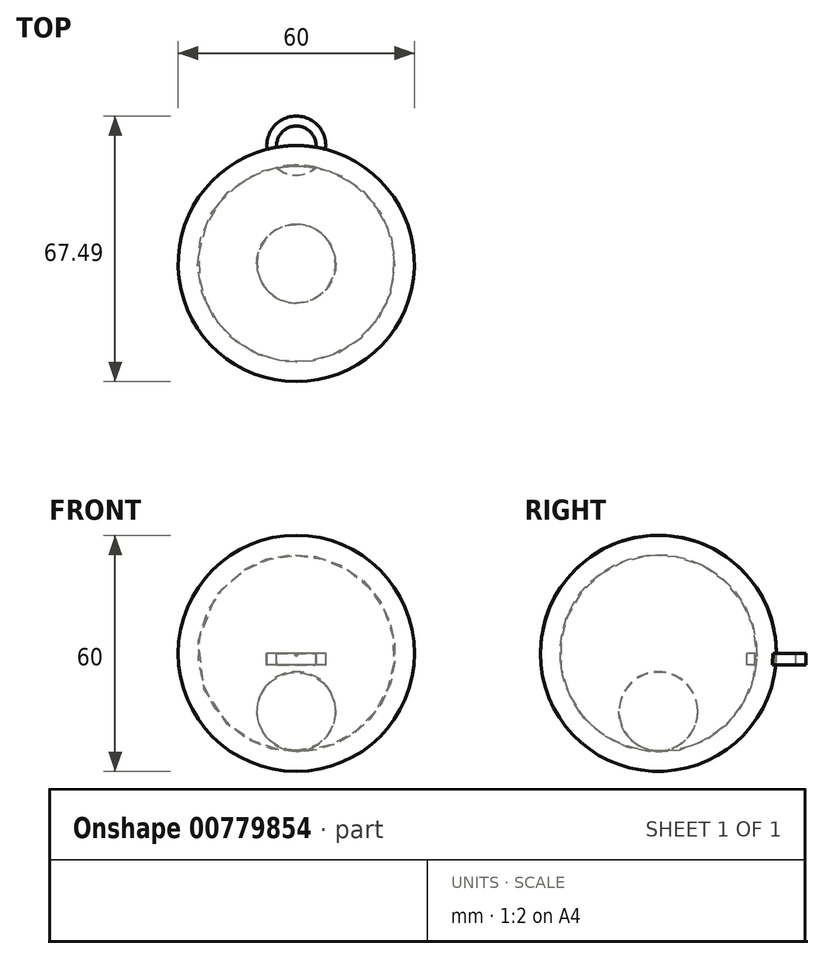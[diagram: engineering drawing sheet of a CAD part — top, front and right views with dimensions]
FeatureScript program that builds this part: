
annotation { "Feature Type Name" : "Feature", "Feature Type Description" : "" }
export const myFeature = defineFeature(function(context is Context, id is Id, definition is map)
    precondition{}
    {
        {
            var Q0;
            Q0=qCreatedBy(makeId("Top.planeOp"),FACE);
            var sketch = newSketch(context, id + "F0", { "sketchPlane" : qUnion([Q0])});
            skArc(sketch, "E0", {"start": v(0, 30) * mm, "mid": v(-30, 0) * mm, "end": v(0, -30) * mm});
            skPoint(sketch, "E1", {"position": v(0, 25) * mm});
            skPoint(sketch, "E2", {"position": v(0, -25) * mm});
            skPoint(sketch, "E3", {"position": v(0, 10) * mm});
            skPoint(sketch, "E4", {"position": v(0, -10) * mm});
            skLineSegment(sketch, "E5", {"start": v(0, 25) * mm, "end": v(0, 30) * mm});
            skLineSegment(sketch, "E6", {"start": v(0, 10) * mm, "end": v(0, -10) * mm});
            skLineSegment(sketch, "E7", {"start": v(0, -25) * mm, "end": v(0, -30) * mm});
            skArc(sketch, "E8", {"start": v(0, 25) * mm, "mid": v(-24.9, 0) * mm, "end": v(0, -25) * mm});
            skArc(sketch, "E9", {"start": v(0, 10) * mm, "mid": v(-9.96, 0) * mm, "end": v(0, -10) * mm});
            skSolve(sketch);
        }
        {
            var Q0;
            Q0=makeQuery(id+"F0.imprint","IMPRINT",FACE,{"disambiguationData":[TD([[makeQuery(id+"F0.imprint","IMPRINT",EDGE,{"derivedFrom":sQuery(id+"F0.wireOp",EDGE,"E0")}),1.0]])]});
            var Q1;
            Q1=makeQuery(id+"F0.imprint","IMPRINT",FACE,{"disambiguationData":[TD([[makeQuery(id+"F0.imprint","IMPRINT",EDGE,{"derivedFrom":sQuery(id+"F0.wireOp",EDGE,"E6")}),-1.0]])]});
            var Q2;
            Q2=sQuery(id+"F0.wireOp",EDGE,"E6");
            revolve(context, id + "F1", {"surfaceOperationType" : NewSurfaceOperationType.NEW, "entities" : qUnion([Q0, Q1]), "axis" : qUnion([Q2]), "revolveType" : RevolveType.FULL});
        }
        {
            var Q0;
            Q0=qCreatedBy(makeId("Top.planeOp"),FACE);
            var sketch = newSketch(context, id + "F2", { "sketchPlane" : qUnion([Q0])});
            skCircle(sketch, "E10", {"center": v(0, 29.99) * mm, "radius": 7.5 * mm});
            skCircle(sketch, "E11", {"center": v(0, 29.99) * mm, "radius": 5 * mm});
            skSolve(sketch);
        }
        {
            var Q0;
            Q0=makeQuery(id+"F2.imprint","IMPRINT",FACE,{"disambiguationData":[TD([[makeQuery(id+"F2.imprint","IMPRINT",EDGE,{"derivedFrom":sQuery(id+"F2.wireOp",EDGE,"E10")}),1.0]])]});
            extrude(context, id + "F3", {"entities" : qUnion([Q0]), "operationType" : NewBodyOperationType.ADD, "oppositeDirection" : true, "depth" : 3 * mm, "offsetDistance" : 25 * mm});
        }
        {
            var Q0;
            Q0=makeQuery(id+"F1.opRevolve","SWEPT_BODY",BODY,{"disambiguationData":[OSD([sQuery(id+"F0.wireOp",EDGE,"E6"),sQuery(id+"F0.wireOp",EDGE,"E9")])]});
            transform(context, id + "F4", {"entities" : qUnion([Q0]), "transformType" : TransformType.TRANSLATION_3D, "dx" : 0 * mm, "dy" : 0 * mm, "dz" : -14.76 * mm, "makeCopy" : false});
        }
    });
